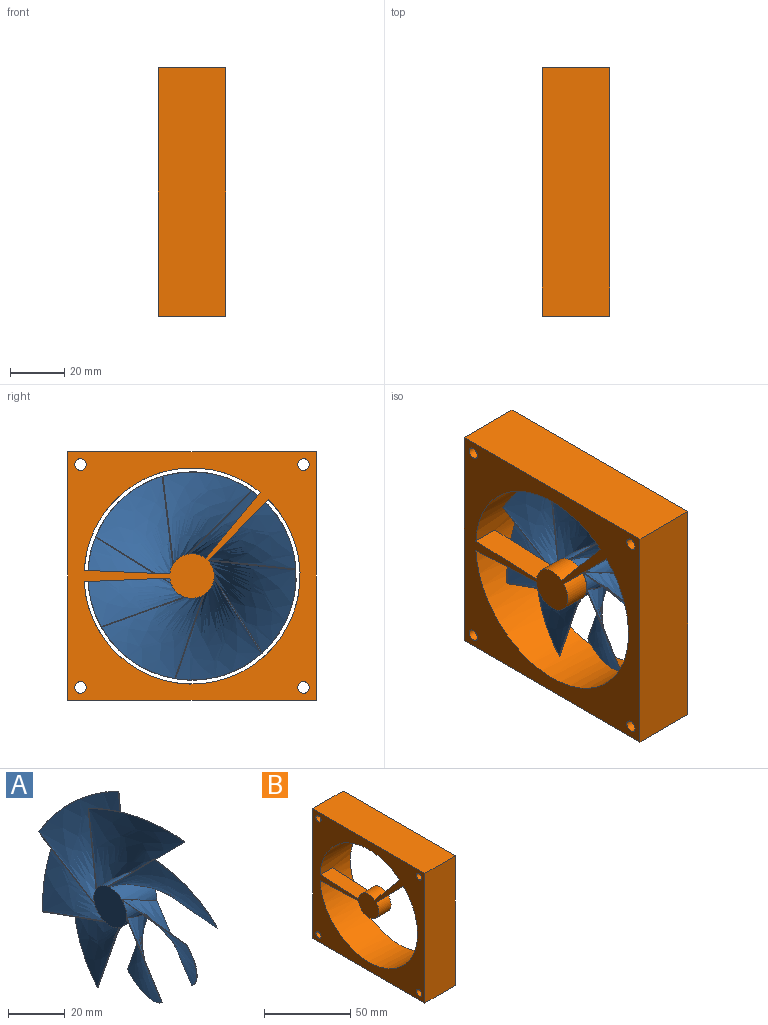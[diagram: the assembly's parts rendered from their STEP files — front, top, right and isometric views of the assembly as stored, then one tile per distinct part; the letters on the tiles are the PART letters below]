
ASSEMBLY  parts=2 mates=1
PART A: 37 faces, bbox 19.7x78.5x78 mm
  f0: cylinder r=8.2mm len=15mm, axis (-1,0,0), area 104.7mm2, adj f7,f8,f30,f33
  f1: cylinder r=8.2mm len=15mm, axis (-1,0,0), area 104.7mm2, adj f7,f8,f26,f29
  f2: cylinder r=8.2mm len=15mm, axis (-1,0,0), area 104.7mm2, adj f7,f8,f22,f25
  f3: cylinder r=8.2mm len=15mm, axis (-1,0,0), area 104.7mm2, adj f7,f8,f18,f21
  f4: cylinder r=8.2mm len=15mm, axis (-1,0,0), area 104.7mm2, adj f7,f8,f14,f17
  f5: cylinder r=8.2mm len=15mm, axis (-1,0,0), area 104.7mm2, adj f7,f8,f10,f13
  f6: cylinder r=8.2mm len=15mm, axis (-1,0,0), area 104.7mm2, adj f7,f8,f9,f34
  f7: plane 75.07x74.25mm, normal (1,0,0), area 280.1mm2, adj f0,f1,f2,f3,f4,f5,f6,f9
  f8: plane 75.05x74.25mm, normal (-1,0,0), area 280.3mm2, adj f0,f1,f2,f3,f4,f5,f6,f9
  f9: bspline ~19.67x8.4mm, area 1mm2, adj f6,f7,f8,f11
  f10: bspline ~40.8x34.9mm, area 823.1mm2, adj f5,f7,f8,f12
  f11: bspline ~40.95x34.96mm, area 827.8mm2, adj f7,f8,f9,f12
  f12: bspline ~33.3x15mm, area 4.8mm2, adj f7,f8,f10,f11
  f13: bspline ~19.67x8.27mm, area 1mm2, adj f5,f7,f8,f15
  f14: bspline ~40.21x39.93mm, area 823.1mm2, adj f4,f7,f8,f16
  f15: bspline ~39.65x29.16mm, area 827.8mm2, adj f7,f8,f13,f16
  f16: bspline ~40.14x19.67mm, area 4.8mm2, adj f7,f8,f14,f15
  f17: bspline ~15x6.73mm, area 1mm2, adj f4,f7,f8,f19
  f18: bspline ~40.36x33.27mm, area 823.1mm2, adj f3,f7,f8,f20
  f19: bspline ~34.52x32.9mm, area 827.8mm2, adj f7,f8,f17,f20
  f20: bspline ~31.24x15mm, area 4.8mm2, adj f7,f8,f18,f19
  f21: bspline ~15x6.18mm, area 1mm2, adj f3,f7,f8,f23
  f22: bspline ~42.35x38.03mm, area 823.1mm2, adj f2,f7,f8,f24
  f23: bspline ~42.36x38.2mm, area 827.8mm2, adj f7,f8,f21,f24
  f24: bspline ~32.38x15mm, area 4.8mm2, adj f7,f8,f22,f23
  f25: bspline ~19.67x9.19mm, area 1mm2, adj f2,f7,f8,f27
  f26: bspline ~41.84x31.41mm, area 823.1mm2, adj f1,f7,f8,f28
  f27: bspline ~38.18x31.23mm, area 827.8mm2, adj f7,f8,f25,f28
  f28: bspline ~27.62x19.4mm, area 4.8mm2, adj f7,f8,f26,f27
  f29: bspline ~19.67x7.35mm, area 1mm2, adj f1,f7,f8,f31
  f30: bspline ~42.65x36.55mm, area 823.1mm2, adj f0,f7,f8,f32
  f31: bspline ~42.73x36.72mm, area 827.8mm2, adj f7,f8,f29,f32
  f32: bspline ~42.93x19.67mm, area 4.8mm2, adj f7,f8,f30,f31
  f33: bspline ~19.67x8.94mm, area 1mm2, adj f0,f7,f8,f35
  f34: bspline ~39.54x28.77mm, area 823.1mm2, adj f6,f7,f8,f36
  f35: bspline ~41.52x35.37mm, area 827.8mm2, adj f7,f8,f33,f36
  f36: bspline ~25.06x22.61mm, area 4.8mm2, adj f7,f8,f34,f35
PART B: 18 faces, bbox 25x92x92 mm
  f0: plane 92x25mm, normal (0,-1,0), area 2300mm2, adj f1,f4,f9,f10
  f1: plane 92x25mm, normal (0,0,-1), area 2300mm2, adj f0,f2,f9,f10
  f2: plane 92x25mm, normal (0,1,0), area 2300mm2, adj f1,f4,f9,f10
  f3: cylinder r=2.15mm len=25mm, axis (-1,0,0), area 337.7mm2, adj f9,f10
  f4: plane 92x25mm, normal (0,0,1), area 2300mm2, adj f0,f2,f9,f10
  f5: cylinder r=40mm len=80mm, axis (-1,0,0), area 6199mm2, adj f9,f10,f12,f13,f15,f16,f17
  f6: cylinder r=2.15mm len=25mm, axis (-1,0,0), area 337.7mm2, adj f9,f10
  f7: cylinder r=2.15mm len=25mm, axis (-1,0,0), area 337.7mm2, adj f9,f10
  f8: cylinder r=2.15mm len=25mm, axis (-1,0,0), area 337.7mm2, adj f9,f10
  f9: plane 92x92mm, normal (1,0,0), area 3379.4mm2, adj f0,f1,f2,f3,f4,f5,f6,f7
  f10: plane 92x92mm, normal (-1,0,0), area 3774.5mm2, adj f0,f1,f2,f3,f4,f5,f6,f7
  f11: cylinder r=8.25mm len=16.47mm, axis (-1,0,0), area 313.1mm2, adj f10,f12,f16,f17
  f12: plane 22.62x22.29mm, normal (0,-0.71,-0.7), area 317.6mm2, adj f5,f10,f11,f17
  f13: plane 24.44x20.28mm, normal (0,0.77,0.64), area 317.6mm2, adj f5,f10,f14,f17
  f14: cylinder r=8.25mm len=13.17mm, axis (-1,0,0), area 175.2mm2, adj f10,f13,f15,f17
  f15: plane 31.73x10mm, normal (0,-0.04,1), area 317.6mm2, adj f5,f10,f14,f17
  f16: plane 31.73x10mm, normal (0,-0.04,-1), area 317.6mm2, adj f5,f10,f11,f17
  f17: plane 68.35x39.29mm, normal (1,0,0), area 395.1mm2, adj f5,f11,f12,f13,f14,f15,f16
PLACE A t=(-41.04,-18.07,-2.43)mm
PLACE B t=(-41.04,-18.07,-2.43)mm
MATE fastened A.f0 <-> B.f5  axis (-1,0,0) through (-31.04,-18.07,-2.43)mm
